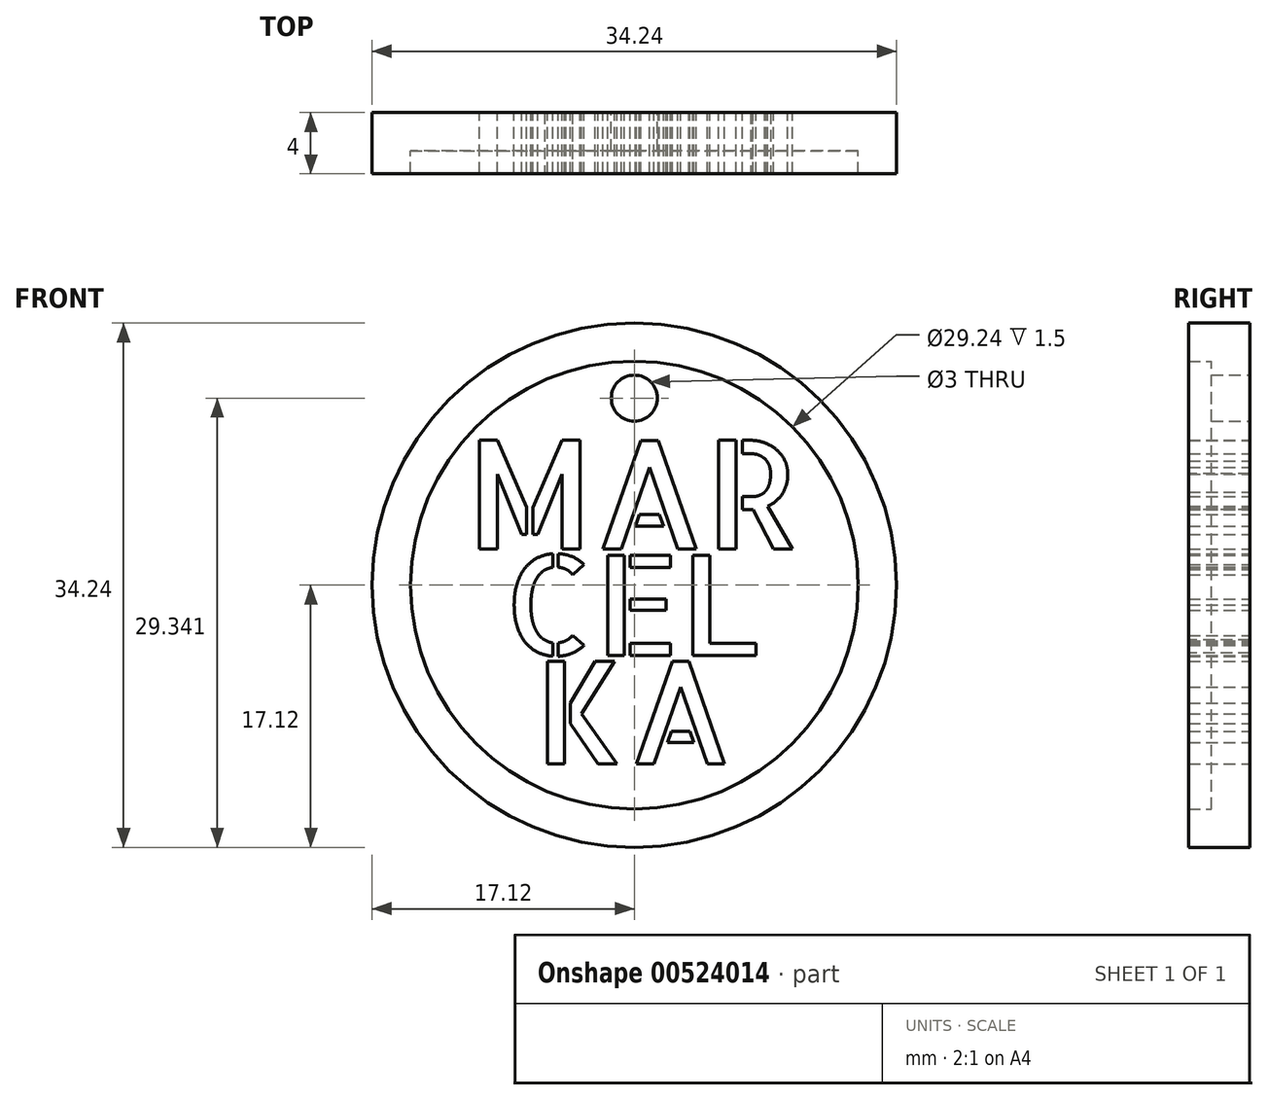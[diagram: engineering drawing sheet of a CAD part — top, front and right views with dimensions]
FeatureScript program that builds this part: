
annotation { "Feature Type Name" : "Feature", "Feature Type Description" : "" }
export const myFeature = defineFeature(function(context is Context, id is Id, definition is map)
    precondition{}
    {
        {
            var Q0;
            Q0=qCreatedBy(makeId("Front.planeOp"),FACE);
            var sketch = newSketch(context, id + "F0", { "sketchPlane" : qUnion([Q0])});
            skText(sketch, "E0", { "text": "MAR", "fontName": "AllertaStencil-Regular.ttf"});
            skText(sketch, "E1", { "text": "CEL", "fontName": "AllertaStencil-Regular.ttf"});
            skText(sketch, "E2", { "text": "KA", "fontName": "AllertaStencil-Regular.ttf"});
            const initialGuessF0  = {"E0": [-0.011, 0.00237, 1, 0, 0.0071], "E1": [-0.00855, -0.0046, 1, 0, 0.00656], "E2": [-0.0065, -0.01166, 1, 0, 0.0067]};
            skSetInitialGuess(sketch, initialGuessF0);
            skSolve(sketch);
        }
        {
            var Q0;
            Q0 = qSketchRegion(id + "F0", true);
            extrude(context, id + "F1", {"entities" : qUnion([Q0]), "depth" : 4 * mm, "offsetDistance" : 25 * mm});
        }
        {
            var Q0;
            Q0=qCreatedBy(makeId("Front.planeOp"),FACE);
            var sketch = newSketch(context, id + "F2", { "sketchPlane" : qUnion([Q0])});
            skPoint(sketch, "E3.middle", {"position": v(0, 0) * mm});
            skCircle(sketch, "E4", {"center": v(0, 0) * mm, "radius": 17.12 * mm});
            skSolve(sketch);
        }
        {
            var Q0;
            Q0=makeQuery(id+"F2.imprint","IMPRINT",FACE,{"disambiguationData":[TD([[makeQuery(id+"F2.imprint","IMPRINT",EDGE,{"derivedFrom":sQuery(id+"F2.wireOp",EDGE,"E3.bottom")}),1.0]])]});
            var Q1;
            Q1=makeQuery(id+"F2.imprint","IMPRINT",FACE,{"disambiguationData":[TD([[makeQuery(id+"F2.imprint","IMPRINT",EDGE,{"derivedFrom":sQuery(id+"F2.wireOp",EDGE,"E4")}),1.0]])]});
            extrude(context, id + "F3", {"entities" : qUnion([Q0, Q1]), "depth" : 4 * mm, "offsetDistance" : 25 * mm});
        }
        {
            var Q0;
            Q0=makeQuery(id+"F3.opExtrude","CAP_FACE",FACE,{"disambiguationData":[OSD([sQuery(id+"F2.wireOp",EDGE,"E4")])],"isStart":false});
            shell(context, id + "F4", {"entities" : qUnion([Q0]), "thickness" : 2.5 * mm});
        }
        {
            var Q0;
            Q0=qCreatedBy(makeId("Front.planeOp"),FACE);
            var sketch = newSketch(context, id + "F5", { "sketchPlane" : qUnion([Q0])});
            skLineSegment(sketch, "E5", {"start": v(0, 0) * mm, "end": v(0, 12.22) * mm});
            skSolve(sketch);
        }
        {
            var Q0;
            Q0=sQuery(id+"F5.wireOp",VERTEX,"pgnarNzG-wreg-w4z7-XcHc-8mOnuien5HOr.end");
            var Q1;
            Q1=sQuery(id+"F5.wireOp",VERTEX,"E5.end");
            var Q2;
            Q2=makeQuery(id+"F3.opExtrude","SWEPT_BODY",BODY,{"disambiguationData":[OSD([sQuery(id+"F2.wireOp",EDGE,"E4")])]});
            hole(context, id + "F6", {"style" : HoleStyle.SIMPLE, "endStyle" : HoleEndStyle.THROUGH, "oppositeDirection" : true, "holeDiameter" : 3 * mm, "isTappedThrough" : true, "tappedDepth" : 12 * mm, "tapClearance" : 3, "locations" : qUnion([Q0, Q1]), "scope" : qUnion([Q2])});
        }
    });
